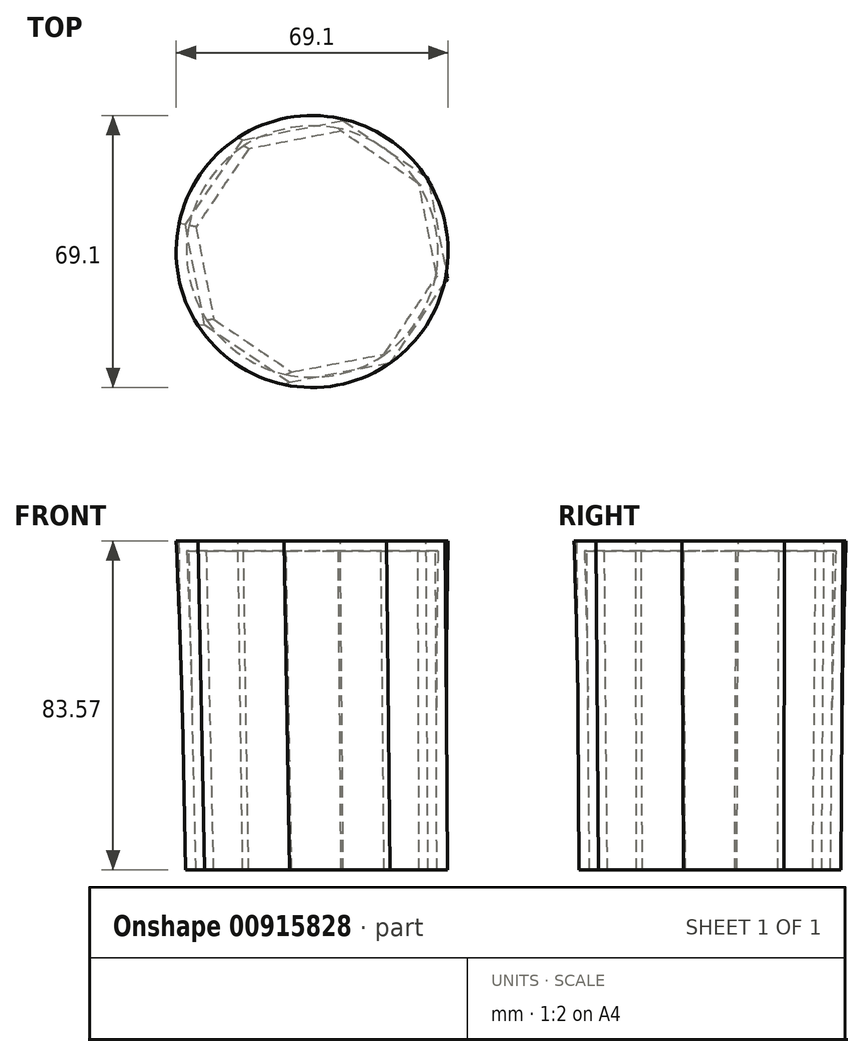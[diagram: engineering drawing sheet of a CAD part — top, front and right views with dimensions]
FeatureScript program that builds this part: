
annotation { "Feature Type Name" : "Feature", "Feature Type Description" : "" }
export const myFeature = defineFeature(function(context is Context, id is Id, definition is map)
    precondition{}
    {
        {
            var Q0;
            Q0=qCreatedBy(makeId("Top.planeOp"),FACE);
            var sketch = newSketch(context, id + "F0", { "sketchPlane" : qUnion([Q0])});
            skCircle(sketch, "E0.cCircle", {"center": v(1.08, 0) * mm, "radius": 31.4 * mm, "construction": true});
            skLineSegment(sketch, "E0.0", {"start": v(-32.2, 6.82) * mm, "end": v(-17.63, 28.36) * mm});
            skLineSegment(sketch, "E0.1", {"start": v(-17.63, 28.36) * mm, "end": v(7.9, 33.29) * mm});
            skLineSegment(sketch, "E0.2", {"start": v(7.9, 33.29) * mm, "end": v(29.45, 18.71) * mm});
            skLineSegment(sketch, "E0.3", {"start": v(29.45, 18.71) * mm, "end": v(34.37, -6.82) * mm});
            skLineSegment(sketch, "E0.4", {"start": v(34.37, -6.82) * mm, "end": v(19.8, -28.36) * mm});
            skLineSegment(sketch, "E0.5", {"start": v(19.8, -28.36) * mm, "end": v(-5.74, -33.29) * mm});
            skLineSegment(sketch, "E0.6", {"start": v(-5.74, -33.29) * mm, "end": v(-27.28, -18.71) * mm});
            skLineSegment(sketch, "E0.7", {"start": v(-27.28, -18.71) * mm, "end": v(-32.2, 6.82) * mm});
            skPoint(sketch, "E0.0.midPoint", {"position": v(-24.91, 17.6) * mm});
            skSolve(sketch);
        }
        {
            var Q0;
            Q0=makeQuery(id+"F0.imprint","IMPRINT",FACE,{"disambiguationData":[TD([[makeQuery(id+"F0.imprint","IMPRINT",EDGE,{"derivedFrom":sQuery(id+"F0.wireOp",EDGE,"E0.0")}),-1.0]])]});
            cPlane(context, id + "F1", {"entities" : qUnion([Q0]), "cplaneType" : CPlaneType.OFFSET, "offset" : 83.57 * mm, "width" : 152.4 * mm, "height" : 152.4 * mm});
        }
        {
            var Q0;
            Q0=qCreatedBy(id+"F1.planeOp",FACE);
            var sketch = newSketch(context, id + "F2", { "sketchPlane" : qUnion([Q0])});
            skCircle(sketch, "E1", {"center": v(0, 0) * mm, "radius": 34.55 * mm});
            skSolve(sketch);
        }
        {
            var Q0;
            Q0=makeQuery(id+"F0.imprint","IMPRINT",FACE,{"disambiguationData":[TD([[makeQuery(id+"F0.imprint","IMPRINT",EDGE,{"derivedFrom":sQuery(id+"F0.wireOp",EDGE,"E0.0")}),-1.0]])]});
            var Q1;
            Q1=makeQuery(id+"F2.imprint","IMPRINT",FACE,{"disambiguationData":[TD([[makeQuery(id+"F2.imprint","IMPRINT",EDGE,{"derivedFrom":sQuery(id+"F2.wireOp",EDGE,"E1")}),1.0]])]});
            loft(context, id + "F3", {"sheetProfilesArray" : [{ "sheetProfileEntities" : qUnion([Q0]) }, { "sheetProfileEntities" : qUnion([Q1]) }]});
        }
        {
            var Q0;
            Q0=makeQuery(id+"F3.opLoft","CAP_FACE",FACE,{"disambiguationData":[OSD([makeQuery(id+"F0.imprint","IMPRINT",FACE,{"disambiguationData":[TD([[makeQuery(id+"F0.imprint","IMPRINT",EDGE,{"derivedFrom":sQuery(id+"F0.wireOp",EDGE,"E0.0")}),-1.0]])]})])],"isStart":true});
            shell(context, id + "F4", {"entities" : qUnion([Q0]), "thickness" : 2.54 * mm});
        }
    });
